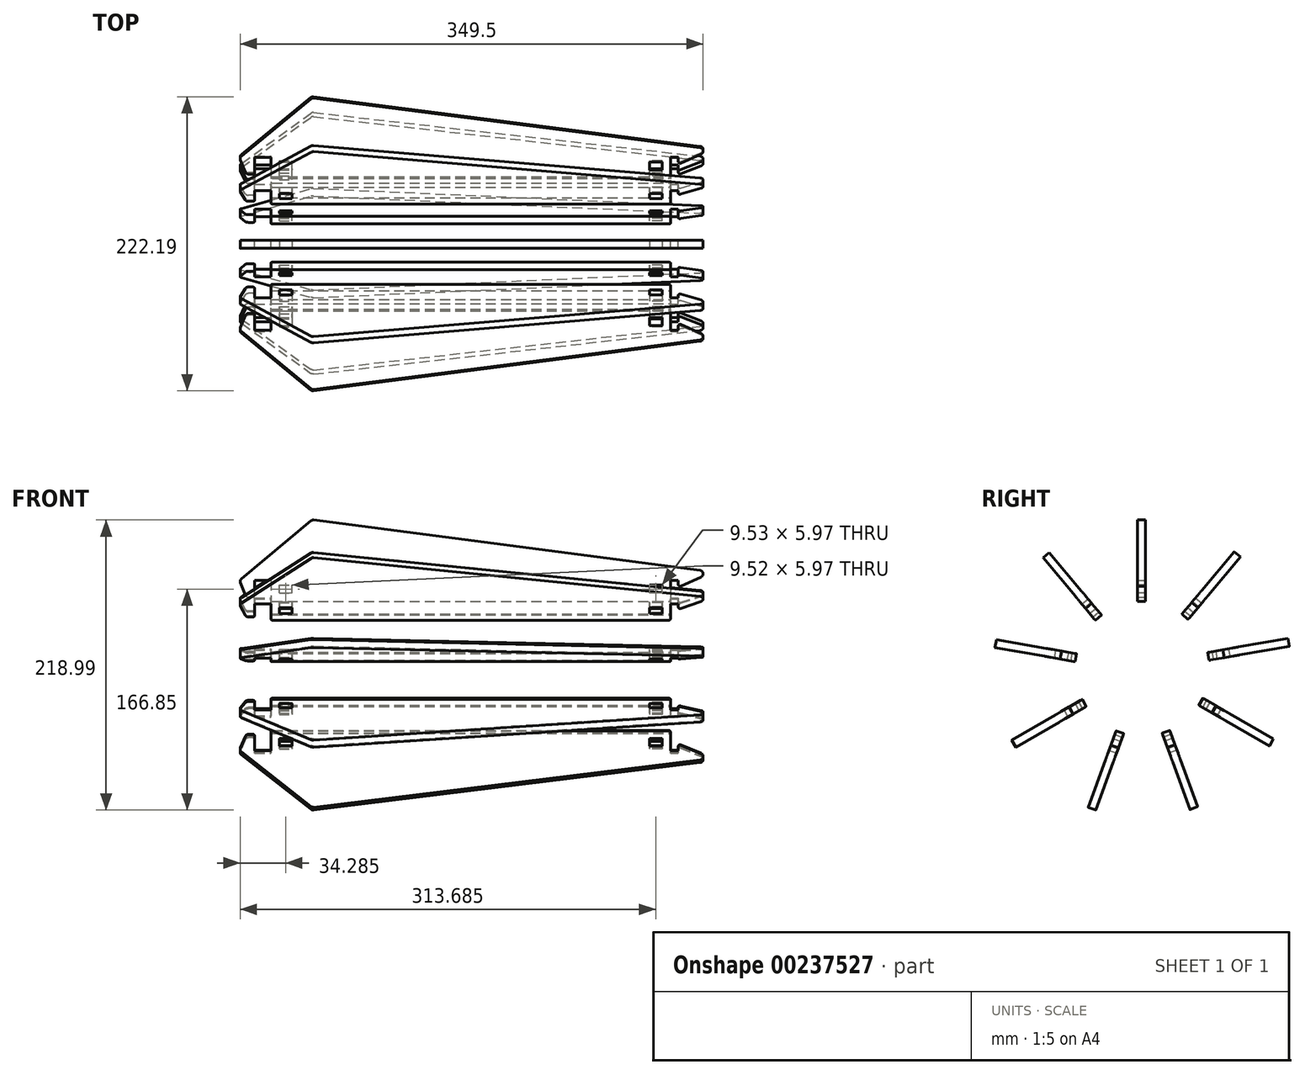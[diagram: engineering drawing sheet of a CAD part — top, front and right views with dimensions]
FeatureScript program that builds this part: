
annotation { "Feature Type Name" : "Feature", "Feature Type Description" : "" }
export const myFeature = defineFeature(function(context is Context, id is Id, definition is map)
    precondition{}
    {
        {
            var Q0;
            Q0=qCreatedBy(makeId("Front.planeOp"),FACE);
            var sketch = newSketch(context, id + "F0", { "sketchPlane" : qUnion([Q0])});
            skLineSegment(sketch, "E0", {"start": v(0, 0) * mm, "end": v(0, 12.7) * mm});
            skLineSegment(sketch, "E1", {"start": v(0, 12.7) * mm, "end": v(12.24, 12.7) * mm});
            skLineSegment(sketch, "E2", {"start": v(0, 0) * mm, "end": v(-6.35, 0) * mm});
            skLineSegment(sketch, "E3", {"start": v(-6.35, 0) * mm, "end": v(-11.43, 12.7) * mm});
            skLineSegment(sketch, "E4", {"start": v(-11.43, 12.7) * mm, "end": v(0, 22.23) * mm});
            skLineSegment(sketch, "E5", {"start": v(0, 22.23) * mm, "end": v(43.43, 58.42) * mm});
            skLineSegment(sketch, "E6", {"start": v(313.87, 12.7) * mm, "end": v(313.87, -3.18) * mm});
            skLineSegment(sketch, "E7", {"start": v(12.24, -3.18) * mm, "end": v(313.87, -3.18) * mm});
            skLineSegment(sketch, "E8", {"start": v(313.87, 12.7) * mm, "end": v(319.84, 12.7) * mm});
            skLineSegment(sketch, "E9", {"start": v(319.84, 12.7) * mm, "end": v(319.84, 7.62) * mm});
            skLineSegment(sketch, "E10", {"start": v(319.84, 7.62) * mm, "end": v(345.24, 19.05) * mm});
            skLineSegment(sketch, "E11", {"start": v(43.43, 58.42) * mm, "end": v(345.24, 19.05) * mm});
            skLineSegment(sketch, "E12", {"start": v(12.24, 12.7) * mm, "end": v(313.87, 12.7) * mm, "construction": true});
            skLineSegment(sketch, "E13", {"start": v(12.24, 12.7) * mm, "end": v(12.24, 12.7) * mm});
            skLineSegment(sketch, "E14", {"start": v(12.24, 12.7) * mm, "end": v(12.24, -3.18) * mm});
            skSolve(sketch);
        }
        {
            var Q0;
            Q0=makeQuery(id+"F0.imprint","IMPRINT",FACE,{"disambiguationData":[TD([[makeQuery(id+"F0.imprint","IMPRINT",EDGE,{"derivedFrom":sQuery(id+"F0.wireOp",EDGE,"E0")}),1.0]])]});
            extrude(context, id + "F1", {"entities" : qUnion([Q0]), "offsetDistance" : 25.4 * mm, "depth" : 6.1 * mm});
        }
        {
            var Q0;
            Q0=makeQuery(id+"F1.opExtrude","SWEPT_FACE",FACE,{"disambiguationData":[OSD([sQuery(id+"F0.wireOp",EDGE,"E14")])]});
            var sketch = newSketch(context, id + "F2", { "sketchPlane" : qUnion([Q0])});
            skPoint(sketch, "E15", {"position": v(2.54, -3.18) * mm});
            skCircle(sketch, "E16", {"center": v(2.54, -53.98) * mm, "radius": 50.8 * mm, "construction": true});
            skSolve(sketch);
        }
        {
            var Q0;
            Q0=makeQuery(id+"F1.opExtrude","CAP_FACE",FACE,{"disambiguationData":[OSD([sQuery(id+"F0.wireOp",EDGE,"E0"),sQuery(id+"F0.wireOp",EDGE,"E1"),sQuery(id+"F0.wireOp",EDGE,"E2"),sQuery(id+"F0.wireOp",EDGE,"E3"),sQuery(id+"F0.wireOp",EDGE,"E4"),sQuery(id+"F0.wireOp",EDGE,"E5"),sQuery(id+"F0.wireOp",EDGE,"E6"),sQuery(id+"F0.wireOp",EDGE,"T48b2aqO-5OnB-VpQv-qECW-1JBLnEAKpYdm"),sQuery(id+"F0.wireOp",EDGE,"E7"),sQuery(id+"F0.wireOp",EDGE,"E8"),sQuery(id+"F0.wireOp",EDGE,"E9"),sQuery(id+"F0.wireOp",EDGE,"E10"),sQuery(id+"F0.wireOp",EDGE,"E11")])],"isStart":false});
            var Q1;
            Q1=makeQuery(id+"F1.opExtrude","CAP_FACE",FACE,{"disambiguationData":[OSD([sQuery(id+"F0.wireOp",EDGE,"E0"),sQuery(id+"F0.wireOp",EDGE,"E1"),sQuery(id+"F0.wireOp",EDGE,"E2"),sQuery(id+"F0.wireOp",EDGE,"E3"),sQuery(id+"F0.wireOp",EDGE,"E4"),sQuery(id+"F0.wireOp",EDGE,"E5"),sQuery(id+"F0.wireOp",EDGE,"E6"),sQuery(id+"F0.wireOp",EDGE,"T48b2aqO-5OnB-VpQv-qECW-1JBLnEAKpYdm"),sQuery(id+"F0.wireOp",EDGE,"E7"),sQuery(id+"F0.wireOp",EDGE,"E8"),sQuery(id+"F0.wireOp",EDGE,"E9"),sQuery(id+"F0.wireOp",EDGE,"E10"),sQuery(id+"F0.wireOp",EDGE,"E11")])],"isStart":true});
            cPlane(context, id + "F3", {"entities" : qUnion([Q0, Q1]), "cplaneType" : CPlaneType.MID_PLANE, "offset" : 25.4 * mm, "width" : 152.4 * mm, "height" : 152.4 * mm});
        }
        {
            var Q0;
            Q0=makeQuery(id+"F1.opExtrude","SWEPT_EDGE",EDGE,{"disambiguationData":[OSD([sQuery(id+"F0.wireOp",EDGE,"E5"),sQuery(id+"F0.wireOp",EDGE,"E11")])]});
            var Q1;
            Q1=makeQuery(id+"F1.opExtrude","SWEPT_EDGE",EDGE,{"disambiguationData":[OSD([sQuery(id+"F0.wireOp",EDGE,"E3"),sQuery(id+"F0.wireOp",EDGE,"E4")])]});
            var Q2;
            Q2=makeQuery(id+"F1.opExtrude","SWEPT_EDGE",EDGE,{"disambiguationData":[OSD([sQuery(id+"F0.wireOp",EDGE,"E2"),sQuery(id+"F0.wireOp",EDGE,"E3")])]});
            var Q3;
            Q3=makeQuery(id+"F1.opExtrude","SWEPT_EDGE",EDGE,{"disambiguationData":[OSD([sQuery(id+"F0.wireOp",EDGE,"E10"),sQuery(id+"F0.wireOp",EDGE,"E11")])]});
            fillet(context, id + "F4", {"entities" : qUnion([Q0, Q1, Q2, Q3]), "radius" : 2.54 * mm, "tangentPropagation" : true, "allowEdgeOverflow" : false});
        }
        {
            var Q0;
            Q0=makeQuery(id+"F1.opExtrude","SWEPT_EDGE",EDGE,{"disambiguationData":[OSD([sQuery(id+"F0.wireOp",EDGE,"E0"),sQuery(id+"F0.wireOp",EDGE,"E2")])]});
            var Q1;
            Q1=makeQuery(id+"F1.opExtrude","SWEPT_EDGE",EDGE,{"disambiguationData":[OSD([sQuery(id+"F0.wireOp",EDGE,"E7"),sQuery(id+"F0.wireOp",EDGE,"E14")])]});
            var Q2;
            Q2=makeQuery(id+"F1.opExtrude","SWEPT_EDGE",EDGE,{"disambiguationData":[OSD([sQuery(id+"F0.wireOp",EDGE,"E9"),sQuery(id+"F0.wireOp",EDGE,"E10")])]});
            var Q3;
            Q3=makeQuery(id+"F1.opExtrude","SWEPT_EDGE",EDGE,{"disambiguationData":[OSD([sQuery(id+"F0.wireOp",EDGE,"E6"),sQuery(id+"F0.wireOp",EDGE,"E7")])]});
            fillet(context, id + "F5", {"entities" : qUnion([Q0, Q1, Q2, Q3]), "radius" : 1.27 * mm, "tangentPropagation" : true, "allowEdgeOverflow" : false});
        }
        {
            var Q0;
            Q0=makeQuery(id+"F1.opExtrude","CAP_FACE",FACE,{"disambiguationData":[OSD([sQuery(id+"F0.wireOp",EDGE,"E0"),sQuery(id+"F0.wireOp",EDGE,"E1"),sQuery(id+"F0.wireOp",EDGE,"E2"),sQuery(id+"F0.wireOp",EDGE,"E3"),sQuery(id+"F0.wireOp",EDGE,"E4"),sQuery(id+"F0.wireOp",EDGE,"E5"),sQuery(id+"F0.wireOp",EDGE,"E6"),sQuery(id+"F0.wireOp",EDGE,"E7"),sQuery(id+"F0.wireOp",EDGE,"E8"),sQuery(id+"F0.wireOp",EDGE,"E9"),sQuery(id+"F0.wireOp",EDGE,"E10"),sQuery(id+"F0.wireOp",EDGE,"E11"),sQuery(id+"F0.wireOp",EDGE,"E14")])],"isStart":false});
            var sketch = newSketch(context, id + "F6", { "sketchPlane" : qUnion([Q0])});
            skLineSegment(sketch, "E17", {"start": v(12.24, 3.17) * mm, "end": v(313.87, 3.17) * mm, "construction": true});
            skPoint(sketch, "E18.oppositeSnap0", {"position": v(0, 9.14) * mm});
            skLineSegment(sketch, "E18.bottom", {"start": v(18.6, 3.17) * mm, "end": v(28.12, 3.17) * mm});
            skLineSegment(sketch, "E18.top", {"start": v(18.6, 9.14) * mm, "end": v(28.12, 9.14) * mm});
            skLineSegment(sketch, "E18.left", {"start": v(18.6, 3.17) * mm, "end": v(18.6, 9.14) * mm});
            skLineSegment(sketch, "E18.right", {"start": v(28.12, 3.17) * mm, "end": v(28.12, 9.14) * mm});
            skLineSegment(sketch, "E19.bottom", {"start": v(307.52, 3.17) * mm, "end": v(298, 3.17) * mm});
            skLineSegment(sketch, "E19.top", {"start": v(307.52, 9.14) * mm, "end": v(298, 9.14) * mm});
            skLineSegment(sketch, "E19.left", {"start": v(307.52, 3.17) * mm, "end": v(307.52, 9.14) * mm});
            skLineSegment(sketch, "E19.right", {"start": v(298, 3.17) * mm, "end": v(298, 9.14) * mm});
            skSolve(sketch);
        }
        {
            var Q0;
            Q0=makeQuery(id+"F6.imprint","IMPRINT",FACE,{"disambiguationData":[TD([[makeQuery(id+"F6.imprint","IMPRINT",EDGE,{"derivedFrom":sQuery(id+"F6.wireOp",EDGE,"E18.bottom")}),1.0]])]});
            var Q1;
            Q1=makeQuery(id+"F6.imprint","IMPRINT",FACE,{"disambiguationData":[TD([[makeQuery(id+"F6.imprint","IMPRINT",EDGE,{"derivedFrom":sQuery(id+"F6.wireOp",EDGE,"E19.bottom")}),-1.0]])]});
            extrude(context, id + "F7", {"entities" : qUnion([Q0, Q1]), "operationType" : NewBodyOperationType.REMOVE, "endBound" : BoundingType.THROUGH_ALL, "oppositeDirection" : true, "depth" : 25.4 * mm, "offsetDistance" : 25.4 * mm});
        }
        {
            var Q0;
            Q0=makeQuery(id+"F1.opExtrude","SWEPT_BODY",BODY,{"disambiguationData":[OSD([sQuery(id+"F0.wireOp",EDGE,"E0"),sQuery(id+"F0.wireOp",EDGE,"E1"),sQuery(id+"F0.wireOp",EDGE,"E2"),sQuery(id+"F0.wireOp",EDGE,"E3"),sQuery(id+"F0.wireOp",EDGE,"E4"),sQuery(id+"F0.wireOp",EDGE,"E5"),sQuery(id+"F0.wireOp",EDGE,"E6"),sQuery(id+"F0.wireOp",EDGE,"T48b2aqO-5OnB-VpQv-qECW-1JBLnEAKpYdm"),sQuery(id+"F0.wireOp",EDGE,"E7"),sQuery(id+"F0.wireOp",EDGE,"E8"),sQuery(id+"F0.wireOp",EDGE,"E9"),sQuery(id+"F0.wireOp",EDGE,"E10"),sQuery(id+"F0.wireOp",EDGE,"E11")])]});
            var Q1;
            Q1=sQuery(id+"F2.wireOp",EDGE,"E16");
            circularPattern(context, id + "F8", {"entities" : qUnion([Q0]), "axis" : qUnion([Q1]), "angle" : 360 * degree, "instanceCount" : 9, "equalSpace" : true});
        }
    });
